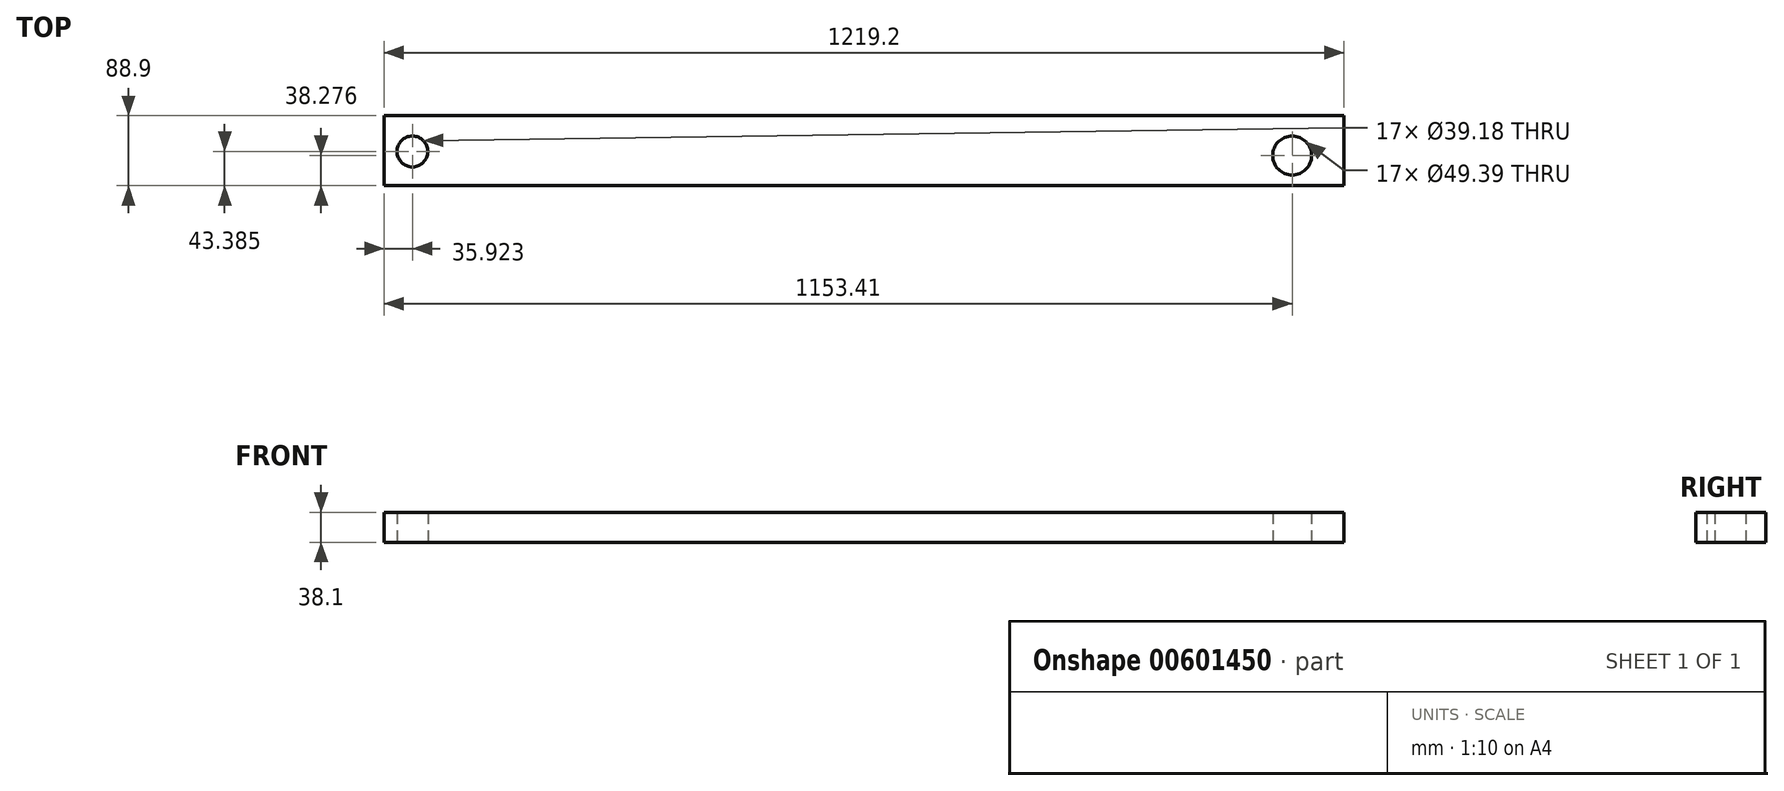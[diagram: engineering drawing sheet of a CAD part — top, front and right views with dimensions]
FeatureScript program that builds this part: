
annotation { "Feature Type Name" : "Feature", "Feature Type Description" : "" }
export const myFeature = defineFeature(function(context is Context, id is Id, definition is map)
    precondition{}
    {
        {
            var Q0;
            Q0=qCreatedBy(makeId("Top.planeOp"),FACE);
            var sketch = newSketch(context, id + "F0", { "sketchPlane" : qUnion([Q0])});
            skLineSegment(sketch, "E0.bottom", {"start": v(0, 0) * mm, "end": v(1219.2, 0) * mm});
            skLineSegment(sketch, "E0.top", {"start": v(0, 88.9) * mm, "end": v(1219.2, 88.9) * mm});
            skLineSegment(sketch, "E0.left", {"start": v(0, 0) * mm, "end": v(0, 88.9) * mm});
            skLineSegment(sketch, "E0.right", {"start": v(1219.2, 0) * mm, "end": v(1219.2, 88.9) * mm});
            skCircle(sketch, "E1", {"center": v(35.92, 43.38) * mm, "radius": 19.59 * mm});
            skCircle(sketch, "E2", {"center": v(1153.41, 38.28) * mm, "radius": 24.7 * mm});
            skSolve(sketch);
        }
        {
            var Q0;
            Q0 = qSketchRegion(id + "F0", true);
            extrude(context, id + "F1", {"entities" : qUnion([Q0]), "depth" : 38.1 * mm, "offsetDistance" : 25.4 * mm});
        }
    });
